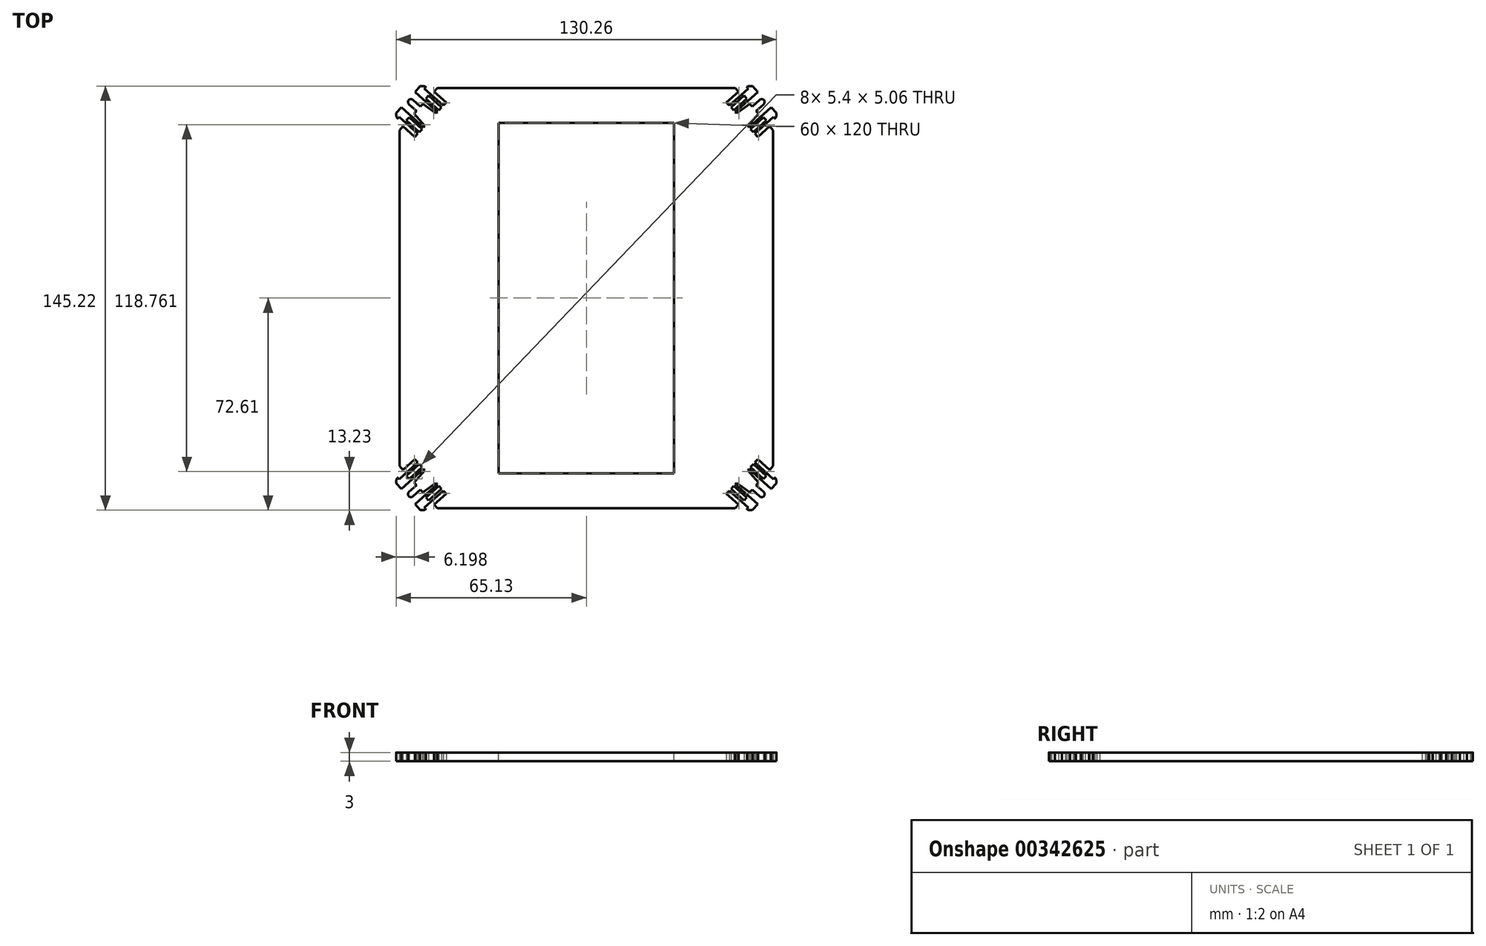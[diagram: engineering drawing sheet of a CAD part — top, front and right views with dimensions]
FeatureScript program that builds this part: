
annotation { "Feature Type Name" : "Feature", "Feature Type Description" : "" }
export const myFeature = defineFeature(function(context is Context, id is Id, definition is map)
    precondition{}
    {
        {
            var Q0;
            Q0=qCreatedBy(makeId("Top.planeOp"),FACE);
            var sketch = newSketch(context, id + "F0", { "sketchPlane" : qUnion([Q0])});
            skLineSegment(sketch, "E0", {"start": v(64, 57.49) * mm, "end": v(64, 0) * mm});
            skLineSegment(sketch, "E1", {"start": v(52.08, 70.72) * mm, "end": v(48, 67.04) * mm});
            skLineSegment(sketch, "E2", {"start": v(48, 67.04) * mm, "end": v(49, 65.92) * mm});
            skLineSegment(sketch, "E3", {"start": v(49, 65.92) * mm, "end": v(55.4, 71.67) * mm});
            skLineSegment(sketch, "E4", {"start": v(58.67, 70.58) * mm, "end": v(51.02, 63.69) * mm});
            skLineSegment(sketch, "E5", {"start": v(51.02, 63.69) * mm, "end": v(51.5, 63.29) * mm});
            skLineSegment(sketch, "E6", {"start": v(51.5, 63.29) * mm, "end": v(56, 66.46) * mm});
            skLineSegment(sketch, "E7", {"start": v(56, 66.46) * mm, "end": v(56.81, 65.55) * mm});
            skLineSegment(sketch, "E8", {"start": v(56.81, 65.55) * mm, "end": v(59.41, 67.89) * mm});
            skLineSegment(sketch, "E9", {"start": v(60.08, 67.15) * mm, "end": v(49.07, 57.23) * mm, "construction": true});
            skLineSegment(sketch, "E10.bottom", {"start": v(49.54, 65.32) * mm, "end": v(50.48, 64.28) * mm});
            skLineSegment(sketch, "E10.top", {"start": v(54, 69.34) * mm, "end": v(54.94, 68.3) * mm});
            skLineSegment(sketch, "E10.left", {"start": v(49.54, 65.32) * mm, "end": v(54, 69.34) * mm});
            skLineSegment(sketch, "E10.right", {"start": v(50.48, 64.28) * mm, "end": v(54.94, 68.3) * mm});
            skLineSegment(sketch, "E11", {"start": v(48, 67.04) * mm, "end": v(52.45, 62.1) * mm, "construction": true});
            skFitSpline(sketch, "E12", {"points": [v(55.4, 71.67) * mm, v(55, 72.26) * mm, v(56.93, 72.51) * mm], "startDerivative": vector(-1.42, 1.73) * mm, "endDerivative": vector(3.75, -1.07) * mm});
            skLineSegment(sketch, "E13", {"start": v(54.5, 75.22) * mm, "end": v(62.16, 66.7) * mm, "construction": true});
            skLineSegment(sketch, "E14", {"start": v(56.93, 72.51) * mm, "end": v(58.67, 70.58) * mm});
            skFitSpline(sketch, "E15.MirrorCS", {"points": [v(64.1, 62.01) * mm, v(64.64, 61.56) * mm, v(65.1, 63.45) * mm], "startDerivative": vector(1.57, -1.6) * mm, "endDerivative": vector(-0.67, 3.84) * mm});
            skLineSegment(sketch, "E16.MirrorCS", {"start": v(58.72, 55.14) * mm, "end": v(57.7, 56.26) * mm});
            skLineSegment(sketch, "E17.MirrorCS", {"start": v(57.17, 56.85) * mm, "end": v(56.23, 57.9) * mm});
            skLineSegment(sketch, "E18.MirrorCS", {"start": v(55.7, 58.49) * mm, "end": v(55.35, 59) * mm});
            skLineSegment(sketch, "E19.MirrorCS", {"start": v(58.72, 55.14) * mm, "end": v(54.27, 60.08) * mm, "construction": true});
            skLineSegment(sketch, "E20.MirrorCS", {"start": v(56.23, 57.9) * mm, "end": v(60.7, 61.9) * mm});
            skLineSegment(sketch, "E21.MirrorCS", {"start": v(62.8, 58.82) * mm, "end": v(58.72, 55.14) * mm});
            skLineSegment(sketch, "E22.MirrorCS", {"start": v(55.35, 59) * mm, "end": v(58.97, 63.15) * mm});
            skLineSegment(sketch, "E23.MirrorCS", {"start": v(63.35, 65.38) * mm, "end": v(55.7, 58.49) * mm});
            skLineSegment(sketch, "E24.MirrorCS", {"start": v(57.7, 56.26) * mm, "end": v(64.1, 62.01) * mm});
            skLineSegment(sketch, "E25.MirrorCS", {"start": v(65.1, 63.45) * mm, "end": v(63.35, 65.38) * mm});
            skLineSegment(sketch, "E26.MirrorCS", {"start": v(58.15, 64.06) * mm, "end": v(60.75, 66.4) * mm});
            skLineSegment(sketch, "E27.MirrorCS", {"start": v(61.63, 60.87) * mm, "end": v(60.7, 61.9) * mm});
            skLineSegment(sketch, "E28.MirrorCS", {"start": v(58.97, 63.15) * mm, "end": v(58.15, 64.06) * mm});
            skLineSegment(sketch, "E29.MirrorCS", {"start": v(57.17, 56.85) * mm, "end": v(61.63, 60.87) * mm});
            skArc(sketch, "E30", {"start": v(59.41, 67.89) * mm, "mid": v(60.83, 67.81) * mm, "end": v(60.75, 66.4) * mm});
            skLineSegment(sketch, "E31.0", {"start": v(54.5, 75.22) * mm, "end": v(56.93, 72.51) * mm, "construction": true});
            skLineSegment(sketch, "E32.0", {"start": v(51.5, 63.29) * mm, "end": v(52.45, 62.1) * mm, "construction": true});
            skLineSegment(sketch, "E33", {"start": v(51, 71.93) * mm, "end": v(0, 72) * mm});
            skLineSegment(sketch, "E34", {"start": v(0, 72) * mm, "end": v(0, 0) * mm});
            skLineSegment(sketch, "E35", {"start": v(0, 0) * mm, "end": v(64, 0) * mm});
            skLineSegment(sketch, "E36", {"start": v(52.08, 70.72) * mm, "end": v(51, 71.93) * mm});
            skLineSegment(sketch, "E37", {"start": v(62.8, 58.82) * mm, "end": v(64, 57.49) * mm});
            skSolve(sketch);
        }
        {
            var Q0;
            Q0=qSketchRegion(id+"F0",true);
            extrude(context, id + "F1", {"entities" : qUnion([Q0]), "depth" : 3 * mm});
        }
        {
            var Q0;
            Q0=makeQuery(id+"F1.opExtrude","SWEPT_BODY",BODY,{"disambiguationData":[OSD([sQuery(id+"F0.wireOp",EDGE,"E0"),sQuery(id+"F0.wireOp",EDGE,"E1"),sQuery(id+"F0.wireOp",EDGE,"E2"),sQuery(id+"F0.wireOp",EDGE,"E3"),sQuery(id+"F0.wireOp",EDGE,"E4"),sQuery(id+"F0.wireOp",EDGE,"E5"),sQuery(id+"F0.wireOp",EDGE,"E6"),sQuery(id+"F0.wireOp",EDGE,"E7"),sQuery(id+"F0.wireOp",EDGE,"E8"),sQuery(id+"F0.wireOp",EDGE,"E10.bottom"),sQuery(id+"F0.wireOp",EDGE,"E10.top"),sQuery(id+"F0.wireOp",EDGE,"E10.left"),sQuery(id+"F0.wireOp",EDGE,"E10.right"),sQuery(id+"F0.wireOp",EDGE,"E12"),sQuery(id+"F0.wireOp",EDGE,"E14"),sQuery(id+"F0.wireOp",EDGE,"E15.MirrorCS"),sQuery(id+"F0.wireOp",EDGE,"E16.MirrorCS"),sQuery(id+"F0.wireOp",EDGE,"E17.MirrorCS"),sQuery(id+"F0.wireOp",EDGE,"E18.MirrorCS"),sQuery(id+"F0.wireOp",EDGE,"73c64eb1-9053-4ded-a230-a61976290448.MirrorCS"),sQuery(id+"F0.wireOp",EDGE,"E20.MirrorCS"),sQuery(id+"F0.wireOp",EDGE,"E21.MirrorCS"),sQuery(id+"F0.wireOp",EDGE,"E22.MirrorCS"),sQuery(id+"F0.wireOp",EDGE,"E23.MirrorCS"),sQuery(id+"F0.wireOp",EDGE,"E24.MirrorCS"),sQuery(id+"F0.wireOp",EDGE,"E25.MirrorCS"),sQuery(id+"F0.wireOp",EDGE,"E26.MirrorCS"),sQuery(id+"F0.wireOp",EDGE,"E27.MirrorCS"),sQuery(id+"F0.wireOp",EDGE,"E28.MirrorCS"),sQuery(id+"F0.wireOp",EDGE,"E29.MirrorCS"),sQuery(id+"F0.wireOp",EDGE,"E30"),sQuery(id+"F0.wireOp",EDGE,"238d3171-18cf-4664-875a-15b81accc3c9"),sQuery(id+"F0.wireOp",EDGE,"7124a334-57a5-4c12-b1ba-874bc8632110.MirrorC"),sQuery(id+"F0.wireOp",EDGE,"E33"),sQuery(id+"F0.wireOp",EDGE,"44bece61-ac72-4aae-9b04-1ec5777349d3"),sQuery(id+"F0.wireOp",EDGE,"E34"),sQuery(id+"F0.wireOp",EDGE,"E35")])]});
            var Q1;
            Q1=makeQuery(id+"F1.opExtrude","SWEPT_FACE",FACE,{"disambiguationData":[OSD([sQuery(id+"F0.wireOp",EDGE,"E34")])]});
            mirror(context, id + "F2", {"operationType" : NewBodyOperationType.ADD, "entities" : qUnion([Q0]), "mirrorPlane" : qUnion([Q1])});
        }
        {
            var Q0;
            Q0=makeQuery(id+"F1.opExtrude","SWEPT_BODY",BODY,{"disambiguationData":[OSD([sQuery(id+"F0.wireOp",EDGE,"E0"),sQuery(id+"F0.wireOp",EDGE,"E1"),sQuery(id+"F0.wireOp",EDGE,"E2"),sQuery(id+"F0.wireOp",EDGE,"E3"),sQuery(id+"F0.wireOp",EDGE,"E4"),sQuery(id+"F0.wireOp",EDGE,"E5"),sQuery(id+"F0.wireOp",EDGE,"E6"),sQuery(id+"F0.wireOp",EDGE,"E7"),sQuery(id+"F0.wireOp",EDGE,"E8"),sQuery(id+"F0.wireOp",EDGE,"E10.bottom"),sQuery(id+"F0.wireOp",EDGE,"E10.top"),sQuery(id+"F0.wireOp",EDGE,"E10.left"),sQuery(id+"F0.wireOp",EDGE,"E10.right"),sQuery(id+"F0.wireOp",EDGE,"E12"),sQuery(id+"F0.wireOp",EDGE,"E14"),sQuery(id+"F0.wireOp",EDGE,"E15.MirrorCS"),sQuery(id+"F0.wireOp",EDGE,"E16.MirrorCS"),sQuery(id+"F0.wireOp",EDGE,"E17.MirrorCS"),sQuery(id+"F0.wireOp",EDGE,"E18.MirrorCS"),sQuery(id+"F0.wireOp",EDGE,"73c64eb1-9053-4ded-a230-a61976290448.MirrorCS"),sQuery(id+"F0.wireOp",EDGE,"E20.MirrorCS"),sQuery(id+"F0.wireOp",EDGE,"E21.MirrorCS"),sQuery(id+"F0.wireOp",EDGE,"E22.MirrorCS"),sQuery(id+"F0.wireOp",EDGE,"E23.MirrorCS"),sQuery(id+"F0.wireOp",EDGE,"E24.MirrorCS"),sQuery(id+"F0.wireOp",EDGE,"E25.MirrorCS"),sQuery(id+"F0.wireOp",EDGE,"E26.MirrorCS"),sQuery(id+"F0.wireOp",EDGE,"E27.MirrorCS"),sQuery(id+"F0.wireOp",EDGE,"E28.MirrorCS"),sQuery(id+"F0.wireOp",EDGE,"E29.MirrorCS"),sQuery(id+"F0.wireOp",EDGE,"E30"),sQuery(id+"F0.wireOp",EDGE,"238d3171-18cf-4664-875a-15b81accc3c9"),sQuery(id+"F0.wireOp",EDGE,"7124a334-57a5-4c12-b1ba-874bc8632110.MirrorC"),sQuery(id+"F0.wireOp",EDGE,"E33"),sQuery(id+"F0.wireOp",EDGE,"44bece61-ac72-4aae-9b04-1ec5777349d3"),sQuery(id+"F0.wireOp",EDGE,"E34"),sQuery(id+"F0.wireOp",EDGE,"E35")])]});
            var Q1;
            {var subQ0=makeQuery(id+"F1.opExtrude","SWEPT_FACE",FACE,{"disambiguationData":[OSD([sQuery(id+"F0.wireOp",EDGE,"E35")])]});Q1=makeQuery(id+"F2.boolean.opBoolean","MERGE",FACE,{"derivedFrom":[subQ0,makeQuery(id+"F2.opPattern","COPY",FACE,{"derivedFrom":subQ0,"instanceName":"1"})]});}
            mirror(context, id + "F3", {"operationType" : NewBodyOperationType.ADD, "entities" : qUnion([Q0]), "mirrorPlane" : qUnion([Q1])});
        }
        {
            var Q0;
            {var subQ0=makeQuery(id+"F1.opExtrude","CAP_FACE",FACE,{"disambiguationData":[OSD([sQuery(id+"F0.wireOp",EDGE,"E0"),sQuery(id+"F0.wireOp",EDGE,"E1"),sQuery(id+"F0.wireOp",EDGE,"E2"),sQuery(id+"F0.wireOp",EDGE,"E3"),sQuery(id+"F0.wireOp",EDGE,"E4"),sQuery(id+"F0.wireOp",EDGE,"E5"),sQuery(id+"F0.wireOp",EDGE,"E6"),sQuery(id+"F0.wireOp",EDGE,"E7"),sQuery(id+"F0.wireOp",EDGE,"E8"),sQuery(id+"F0.wireOp",EDGE,"E10.bottom"),sQuery(id+"F0.wireOp",EDGE,"E10.top"),sQuery(id+"F0.wireOp",EDGE,"E10.left"),sQuery(id+"F0.wireOp",EDGE,"E10.right"),sQuery(id+"F0.wireOp",EDGE,"E12"),sQuery(id+"F0.wireOp",EDGE,"E14"),sQuery(id+"F0.wireOp",EDGE,"E15.MirrorCS"),sQuery(id+"F0.wireOp",EDGE,"E16.MirrorCS"),sQuery(id+"F0.wireOp",EDGE,"E17.MirrorCS"),sQuery(id+"F0.wireOp",EDGE,"E18.MirrorCS"),sQuery(id+"F0.wireOp",EDGE,"73c64eb1-9053-4ded-a230-a61976290448.MirrorCS"),sQuery(id+"F0.wireOp",EDGE,"E20.MirrorCS"),sQuery(id+"F0.wireOp",EDGE,"E21.MirrorCS"),sQuery(id+"F0.wireOp",EDGE,"E22.MirrorCS"),sQuery(id+"F0.wireOp",EDGE,"E23.MirrorCS"),sQuery(id+"F0.wireOp",EDGE,"E24.MirrorCS"),sQuery(id+"F0.wireOp",EDGE,"E25.MirrorCS"),sQuery(id+"F0.wireOp",EDGE,"E26.MirrorCS"),sQuery(id+"F0.wireOp",EDGE,"E27.MirrorCS"),sQuery(id+"F0.wireOp",EDGE,"E28.MirrorCS"),sQuery(id+"F0.wireOp",EDGE,"E29.MirrorCS"),sQuery(id+"F0.wireOp",EDGE,"E30"),sQuery(id+"F0.wireOp",EDGE,"238d3171-18cf-4664-875a-15b81accc3c9"),sQuery(id+"F0.wireOp",EDGE,"7124a334-57a5-4c12-b1ba-874bc8632110.MirrorC"),sQuery(id+"F0.wireOp",EDGE,"E33"),sQuery(id+"F0.wireOp",EDGE,"44bece61-ac72-4aae-9b04-1ec5777349d3"),sQuery(id+"F0.wireOp",EDGE,"E34"),sQuery(id+"F0.wireOp",EDGE,"E35")])],"isStart":false});var subQ1=makeQuery(id+"F2.boolean.opBoolean","MERGE",FACE,{"derivedFrom":[subQ0,makeQuery(id+"F2.opPattern","COPY",FACE,{"derivedFrom":subQ0,"instanceName":"1"})]});Q0=makeQuery(id+"F3.boolean.opBoolean","MERGE",FACE,{"derivedFrom":[subQ1,makeQuery(id+"F3.opPattern","COPY",FACE,{"derivedFrom":subQ1,"instanceName":"1"})]});}
            var sketch = newSketch(context, id + "F4", { "sketchPlane" : qUnion([Q0])});
            skLineSegment(sketch, "E38.bottom", {"start": v(30, 60) * mm, "end": v(-30, 60) * mm});
            skLineSegment(sketch, "E38.top", {"start": v(30, -60) * mm, "end": v(-30, -60) * mm});
            skLineSegment(sketch, "E38.left", {"start": v(30, 60) * mm, "end": v(30, -60) * mm});
            skLineSegment(sketch, "E38.right", {"start": v(-30, 60) * mm, "end": v(-30, -60) * mm});
            skPoint(sketch, "E38.middle", {"position": v(0, 0) * mm});
            skSolve(sketch);
        }
        {
            var Q0;
            Q0=qSketchRegion(id+"F4",true);
            extrude(context, id + "F5", {"entities" : qUnion([Q0]), "operationType" : NewBodyOperationType.REMOVE, "oppositeDirection" : true, "depth" : 3 * mm});
        }
    });
